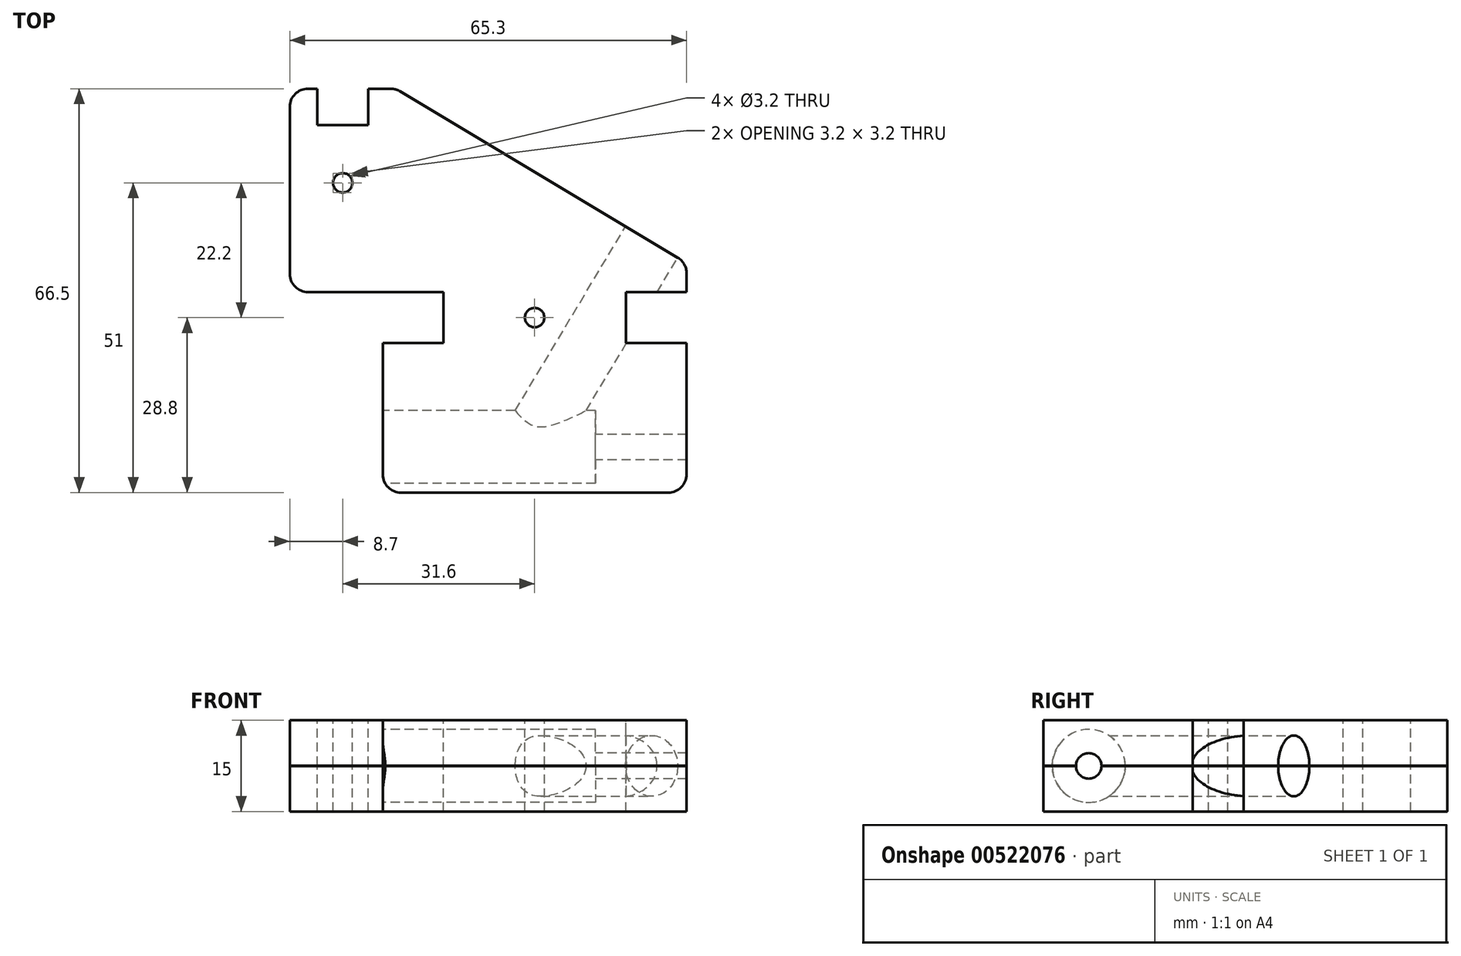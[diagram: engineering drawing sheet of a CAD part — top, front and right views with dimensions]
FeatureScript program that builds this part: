
annotation { "Feature Type Name" : "Feature", "Feature Type Description" : "" }
export const myFeature = defineFeature(function(context is Context, id is Id, definition is map)
    precondition{}
    {
        {
            var Q0;
            Q0=qCreatedBy(makeId("Top.planeOp"),FACE);
            var sketch = newSketch(context, id + "F0", { "sketchPlane" : qUnion([Q0])});
            skLineSegment(sketch, "E0", {"start": v(40, 0) * mm, "end": v(40, 3.1) * mm});
            skLineSegment(sketch, "E1", {"start": v(38.54, 5.67) * mm, "end": v(-7.19, 33.07) * mm});
            skLineSegment(sketch, "E2", {"start": v(-8.73, 33.5) * mm, "end": v(-12.4, 33.5) * mm});
            skLineSegment(sketch, "E3", {"start": v(-12.4, 33.5) * mm, "end": v(-12.4, 27.5) * mm});
            skLineSegment(sketch, "E4", {"start": v(-12.4, 27.5) * mm, "end": v(-20.8, 27.5) * mm});
            skLineSegment(sketch, "E5", {"start": v(-20.8, 27.5) * mm, "end": v(-20.8, 33.5) * mm});
            skLineSegment(sketch, "E6", {"start": v(-20.8, 33.5) * mm, "end": v(-22.3, 33.5) * mm});
            skLineSegment(sketch, "E7", {"start": v(-25.3, 30.5) * mm, "end": v(-25.3, 3) * mm});
            skLineSegment(sketch, "E8", {"start": v(-22.3, 0) * mm, "end": v(0, 0) * mm});
            skLineSegment(sketch, "E9", {"start": v(0, 0) * mm, "end": v(0, -8.4) * mm});
            skLineSegment(sketch, "E10", {"start": v(0, -8.4) * mm, "end": v(-10, -8.4) * mm});
            skLineSegment(sketch, "E11", {"start": v(40, -30) * mm, "end": v(40, -8.4) * mm});
            skLineSegment(sketch, "E12", {"start": v(40, -8.4) * mm, "end": v(30, -8.4) * mm});
            skLineSegment(sketch, "E13", {"start": v(30, -8.4) * mm, "end": v(30, 0) * mm});
            skLineSegment(sketch, "E14", {"start": v(30, 0) * mm, "end": v(40, 0) * mm});
            skPoint(sketch, "E15.visualSharp", {"position": v(-25.3, 0) * mm});
            skArc(sketch, "E15.filletArc", {"start": v(-25.3, 3) * mm, "mid": v(-24.42, 0.88) * mm, "end": v(-22.3, 0) * mm});
            skPoint(sketch, "E16.visualSharp", {"position": v(-25.3, 33.5) * mm});
            skArc(sketch, "E16.filletArc", {"start": v(-22.3, 33.5) * mm, "mid": v(-24.42, 32.62) * mm, "end": v(-25.3, 30.5) * mm});
            skPoint(sketch, "E17.visualSharp", {"position": v(40, 4.8) * mm});
            skArc(sketch, "E17.filletArc", {"start": v(40, 3.1) * mm, "mid": v(39.61, 4.58) * mm, "end": v(38.54, 5.67) * mm});
            skPoint(sketch, "E18.visualSharp", {"position": v(-7.9, 33.5) * mm});
            skArc(sketch, "E18.filletArc", {"start": v(-7.19, 33.07) * mm, "mid": v(-7.93, 33.4) * mm, "end": v(-8.73, 33.5) * mm});
            skCircle(sketch, "E19", {"center": v(-16.6, 18) * mm, "radius": 1.6 * mm});
            skLineSegment(sketch, "E20", {"start": v(-16.6, 27.5) * mm, "end": v(-16.6, 18) * mm, "construction": true});
            skLineSegment(sketch, "E21", {"start": v(0, -4.2) * mm, "end": v(30, -4.2) * mm, "construction": true});
            skCircle(sketch, "E22", {"center": v(15, -4.2) * mm, "radius": 1.6 * mm});
            skLineSegment(sketch, "E23", {"start": v(-10, -8.4) * mm, "end": v(-10, -30) * mm});
            skLineSegment(sketch, "E24", {"start": v(-7, -33) * mm, "end": v(37, -33) * mm});
            skPoint(sketch, "E25.visualSharp", {"position": v(-10, -33) * mm});
            skArc(sketch, "E25.filletArc", {"start": v(-10, -30) * mm, "mid": v(-9.12, -32.12) * mm, "end": v(-7, -33) * mm});
            skPoint(sketch, "E26.visualSharp", {"position": v(40, -33) * mm});
            skArc(sketch, "E26.filletArc", {"start": v(37, -33) * mm, "mid": v(39.12, -32.12) * mm, "end": v(40, -30) * mm});
            skSolve(sketch);
        }
        {
            var Q0;
            Q0=makeQuery(id+"F0.imprint","IMPRINT",FACE,{"disambiguationData":[TD([[makeQuery(id+"F0.imprint","IMPRINT",EDGE,{"derivedFrom":sQuery(id+"F0.wireOp",EDGE,"E0")}),1.0]])]});
            extrude(context, id + "F1", {"entities" : qUnion([Q0]), "oppositeDirection" : true, "depth" : 15 * mm, "offsetDistance" : 25 * mm});
        }
        {
            var Q0;
            Q0=makeQuery(id+"F1.opExtrude","SWEPT_FACE",FACE,{"disambiguationData":[OSD([sQuery(id+"F0.wireOp",EDGE,"E23")])]});
            var sketch = newSketch(context, id + "F2", { "sketchPlane" : qUnion([Q0])});
            skCircle(sketch, "E27", {"center": v(25.5, -7.5) * mm, "radius": 6 * mm});
            skCircle(sketch, "E28", {"center": v(25.5, -7.5) * mm, "radius": 2.1 * mm});
            skLineSegment(sketch, "E29", {"start": v(30, -7.5) * mm, "end": v(25.5, -7.5) * mm, "construction": true});
            skSolve(sketch);
        }
        {
            var Q0;
            Q0 = qSketchRegion(id + "F2", true);
            extrude(context, id + "F3", {"entities" : qUnion([Q0]), "operationType" : NewBodyOperationType.REMOVE, "oppositeDirection" : true, "depth" : 35 * mm, "offsetDistance" : 25 * mm});
        }
        {
            var Q0;
            Q0=makeQuery(id+"F2.imprint","IMPRINT",FACE,{"disambiguationData":[TD([[makeQuery(id+"F2.imprint","IMPRINT",EDGE,{"derivedFrom":sQuery(id+"F2.wireOp",EDGE,"E28")}),1.0]])]});
            extrude(context, id + "F4", {"entities" : qUnion([Q0]), "operationType" : NewBodyOperationType.REMOVE, "oppositeDirection" : true, "depth" : 60 * mm, "offsetDistance" : 25 * mm});
        }
        {
            var Q0;
            Q0=makeQuery(id+"F1.opExtrude","SWEPT_FACE",FACE,{"disambiguationData":[OSD([sQuery(id+"F0.wireOp",EDGE,"E1")])]});
            var sketch = newSketch(context, id + "F5", { "sketchPlane" : qUnion([Q0])});
            skLineSegment(sketch, "E30", {"start": v(-30.15, -7.5) * mm, "end": v(23.16, -7.5) * mm, "construction": true});
            skCircle(sketch, "E31", {"center": v(-25.15, -7.5) * mm, "radius": 5 * mm});
            skSolve(sketch);
        }
        {
            var Q0;
            Q0=makeQuery(id+"F5.imprint","IMPRINT",FACE,{"disambiguationData":[TD([[makeQuery(id+"F5.imprint","IMPRINT",EDGE,{"derivedFrom":sQuery(id+"F5.wireOp",EDGE,"E31")}),1.0]])]});
            extrude(context, id + "F6", {"entities" : qUnion([Q0]), "operationType" : NewBodyOperationType.REMOVE, "oppositeDirection" : true, "depth" : 41 * mm, "offsetDistance" : 25 * mm});
        }
        {
            var Q0;
            Q0=makeQuery(id+"F1.opExtrude","SWEPT_FACE",FACE,{"disambiguationData":[OSD([sQuery(id+"F0.wireOp",EDGE,"E7")])]});
            var sketch = newSketch(context, id + "F7", { "sketchPlane" : qUnion([Q0])});
            skLineSegment(sketch, "E32.bottom", {"start": v(-48, -7.55) * mm, "end": v(42, -7.55) * mm});
            skLineSegment(sketch, "E32.top", {"start": v(-48, -7.45) * mm, "end": v(42, -7.45) * mm});
            skLineSegment(sketch, "E32.left", {"start": v(-48, -7.55) * mm, "end": v(-48, -7.45) * mm});
            skLineSegment(sketch, "E32.right", {"start": v(42, -7.55) * mm, "end": v(42, -7.45) * mm});
            skPoint(sketch, "E32.middle", {"position": v(-3, -7.5) * mm});
            skSolve(sketch);
        }
        {
            var Q0;
            {var subQ0=sQuery(id+"F7.wireOp",EDGE,"E32.right");Q0=makeQuery(id+"F7.imprint","IMPRINT",FACE,{"disambiguationData":[TD([[makeQuery(id+"F7.imprint","IMPRINT",EDGE,{"derivedFrom":subQ0}),1.0]])]});}
            var Q1;
            {var subQ0=sQuery(id+"F7.wireOp",EDGE,"E32.bottom");var subQ1=sQuery(id+"F0.wireOp",EDGE,"E7");var subQ2=makeQuery(id+"F1.opExtrude","SWEPT_EDGE",EDGE,{"disambiguationData":[OSD([subQ1,sQuery(id+"F0.wireOp",EDGE,"E16.filletArc")])]});var subQ3=makeQuery(id+"F7.imprint","INTERSECT",VERTEX,{"derivedFrom":[subQ2,subQ0]});Q1=makeQuery(id+"F7.imprint","IMPRINT",FACE,{"disambiguationData":[TD([[makeQuery(id+"F7.imprint","IMPRINT",EDGE,{"disambiguationData":[TD([[subQ3,-1.0]])],"derivedFrom":subQ0}),1.0]])]});}
            var Q2;
            {var subQ0=sQuery(id+"F7.wireOp",EDGE,"E32.left");Q2=makeQuery(id+"F7.imprint","IMPRINT",FACE,{"disambiguationData":[TD([[makeQuery(id+"F7.imprint","IMPRINT",EDGE,{"derivedFrom":subQ0}),-1.0]])]});}
            extrude(context, id + "F8", {"entities" : qUnion([Q0, Q1, Q2]), "operationType" : NewBodyOperationType.REMOVE, "oppositeDirection" : true, "depth" : 70 * mm, "offsetDistance" : 25 * mm});
        }
    });
